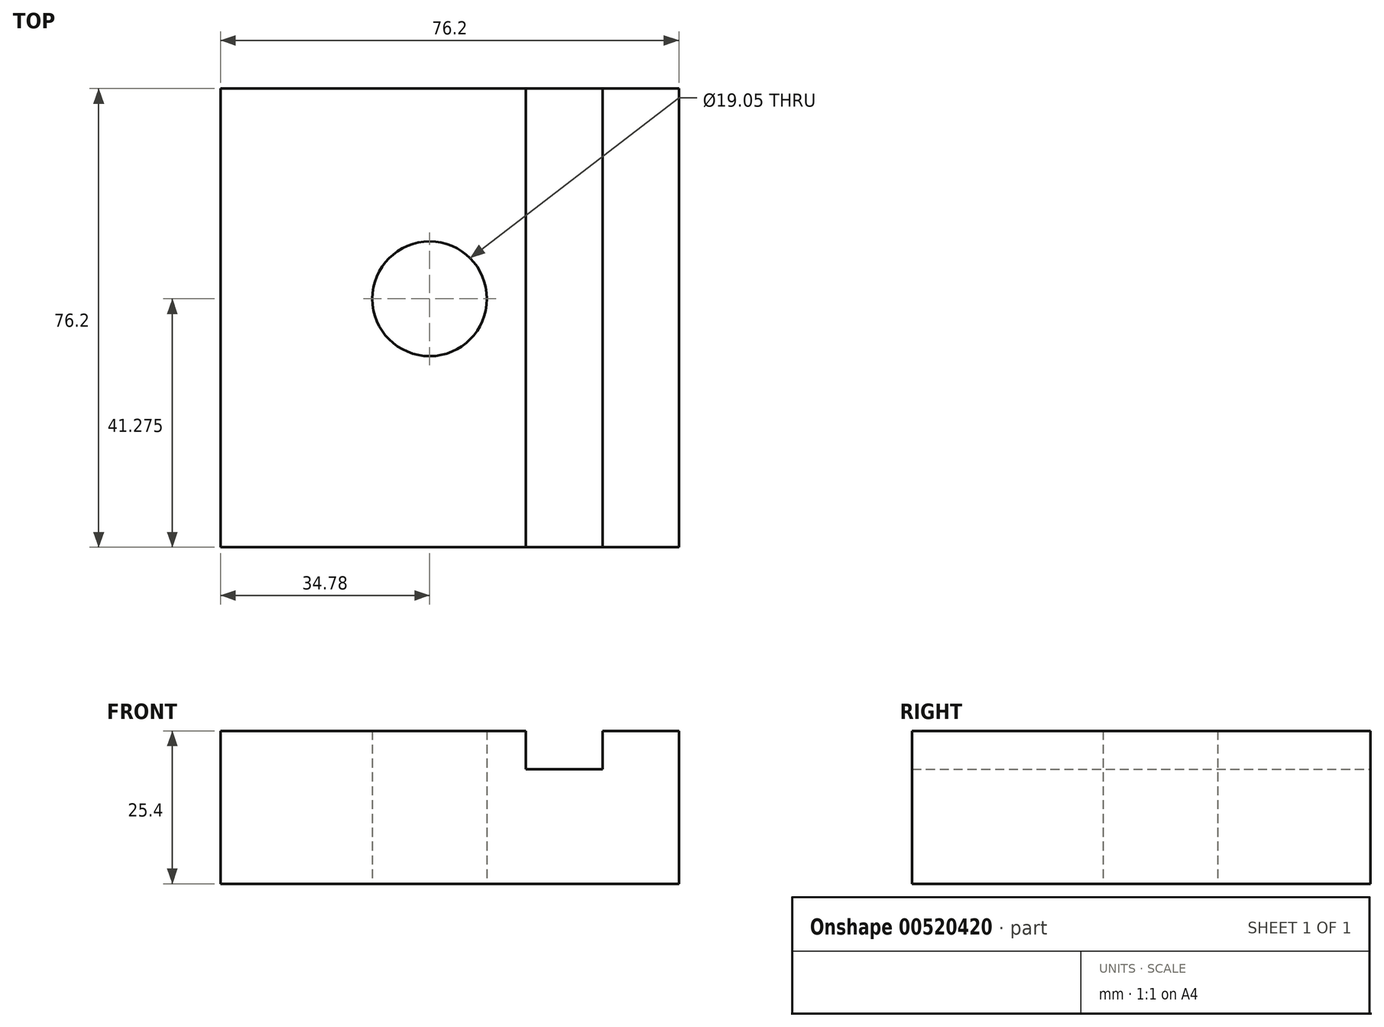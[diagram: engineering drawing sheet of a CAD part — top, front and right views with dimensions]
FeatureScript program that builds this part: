
annotation { "Feature Type Name" : "Feature", "Feature Type Description" : "" }
export const myFeature = defineFeature(function(context is Context, id is Id, definition is map)
    precondition{}
    {
        {
            var Q0;
            Q0=qCreatedBy(makeId("Front.planeOp"),FACE);
            var sketch = newSketch(context, id + "F0", { "sketchPlane" : qUnion([Q0])});
            skLineSegment(sketch, "E0", {"start": v(25.4, 0) * mm, "end": v(-50.8, 0) * mm});
            skLineSegment(sketch, "E1", {"start": v(-50.8, 0) * mm, "end": v(-50.8, 25.4) * mm});
            skLineSegment(sketch, "E2", {"start": v(-50.8, 25.4) * mm, "end": v(0, 25.4) * mm});
            skLineSegment(sketch, "E3", {"start": v(0, 25.4) * mm, "end": v(0, 19.05) * mm});
            skLineSegment(sketch, "E4", {"start": v(0, 19.05) * mm, "end": v(12.7, 19.05) * mm});
            skLineSegment(sketch, "E5", {"start": v(12.7, 19.05) * mm, "end": v(12.7, 25.4) * mm});
            skLineSegment(sketch, "E6", {"start": v(12.7, 25.4) * mm, "end": v(25.4, 25.4) * mm});
            skLineSegment(sketch, "E7", {"start": v(25.4, 25.4) * mm, "end": v(25.4, 0) * mm});
            skSolve(sketch);
        }
        {
            var Q0;
            Q0=makeQuery(id+"F0.imprint","IMPRINT",FACE,{"disambiguationData":[TD([[makeQuery(id+"F0.imprint","IMPRINT",EDGE,{"derivedFrom":sQuery(id+"F0.wireOp",EDGE,"E0")}),-1.0]])]});
            extrude(context, id + "F1", {"entities" : qUnion([Q0]), "depth" : 76.2 * mm, "offsetDistance" : 25.4 * mm});
        }
        {
            var Q0;
            Q0=qCreatedBy(makeId("Top.planeOp"),FACE);
            var sketch = newSketch(context, id + "F2", { "sketchPlane" : qUnion([Q0])});
            skCircle(sketch, "E8", {"center": v(-16.02, -34.93) * mm, "radius": 9.52 * mm});
            skSolve(sketch);
        }
        {
            var Q0;
            Q0=qSketchRegion(id+"F2",true);
            extrude(context, id + "F3", {"entities" : qUnion([Q0]), "operationType" : NewBodyOperationType.REMOVE, "depth" : 76.2 * mm, "offsetDistance" : 25.4 * mm});
        }
    });
